# Revit family: BC_Hitachi_Cassette-RCI-FSR-1.0-6.0_LOD200
name_source: partatom
category: Mechanical Equipment
revit_build: Autodesk Revit 2018 (Build: 20170223_1515(x64)
units: mm (PartAtom-declared; Revit-internal decimal feet)

## family parameters
Cut with Voids When Loaded = No
Host = Face
OmniClass Number = 23.75.70.00
OmniClass Title = HVAC Distribution Devices
Part Type = Normal
Room Calculation Point = No
Round Connector Dimension = Use Diameter
Shared = No

## types (8) — shared parameters
BC_OBJECT_ID = 209116
BC_OBJECT_VERSION = #9
Color = Neutral white (4.56Y8.85/0.38)
Default Elevation = 1219.20 mm
Description = Standard Cassette 800*800.Individual control setting for each louver. Suitable up to 4,2 m height under ceiling . Optional motion sensor
Facade Width = 950.00 mm
Face Depth = 40.00 mm
Face Height = 950.00 mm
Frequency = 50 Hz
Manufacturer = Hitachi Air Conditioning Europe SAS
MasterFormat = Indoor Central-Station Air-Handling Units
Masterformat Code = 23 73 00
Maximal Input Power = 0 kW
Maximum AC Voltage = 253 V
Minimum AC Voltage = 207 V
Model = Cassette 800 x 800 RCI FSR
Name BIM&CO = Indoor Unit
Nominal Voltage = 230 V
Number of Poles = 1
OmniClass code = 23-33 25 00
OmniClass description = Air Handling Units
Outlet Diameter = 32.00 mm
Overall height = 840.00 mm
Overall width = 840.00 mm
Refrigerant Type = R410A / R32
Service space = Yes
Uniformat = Distribution Systems
Uniformat code = D3040
Usage Current = 5 A

## per-type parameters (varying)
| type | Acoustic Pressure Level Maxi | Acoustic Pressure Level Mini | Air Flow (HiH/Hi/Me/low) m3/min | BC_VARIANT_ID | Cooling Capacity | Fan motor input | Gas Diameter | Heating Capacity | Liquid Diameter | Mass | Maximum Air Flow | Minimum Air Flow | Overall depth | Product Code | Sound power at rated load |
| RCI-2.0FSR | 37 | 27 | 21 / 17 / 14 / 11 | 508752 | 5 kW | 57 W | 12.70 mm | 6 kW | 6.35 mm | 27.50 kg | 21000.0 L/min | 11000.0 L/min | 248.00 mm | 70405303 | 55 |
| RCI-2.5FSR | 42 | 28 | 27 / 23 / 18 / 14 | 508747 | 6 kW | 57 W | 15.88 mm | 6 kW | 9.52 mm | 28.50 kg | 27000.0 L/min | 14000.0 L/min | 248.00 mm | 70405304 | 56 |
| RCI-6.0FSR | 48 | 37 | 37 / 35 / 28 / 22 | 508746 | 14 kW | 127 W | 15.88 mm | 16 kW | 9.52 mm | 32.50 kg | 37000.0 L/min | 22000.0 L/min | 298.00 mm | 70405309 | 65 |
| RCI-5.0FSR | 48 | 35 | 37 / 33 / 26 / 21 | 508750 | 13 kW | 127 W | 15.88 mm | 14 kW | 9.52 mm | 32.50 kg | 37000.0 L/min | 21000.0 L/min | 298.00 mm | 70405308 | 64 |
| RCI-4.0FSR | 48 | 33 | 37 / 31 / 24 / 20 | 508751 | 10 kW | 127 W | 15.88 mm | 11 kW | 9.52 mm | 32.50 kg | 37000.0 L/min | 20000.0 L/min | 298.00 mm | 70405307 | 64 |
| RCI-3.0FSR | 42 | 28 | 27 / 23 / 18 / 14 | 508748 | 7 kW | 57 W | 15.88 mm | 8 kW | 9.52 mm | 32.50 kg | 27000.0 L/min | 14000.0 L/min | 298.00 mm | 70405305 | 57 |
| RCI-1.5FSR | 35 | 27 | 21 / 17 / 14 / 11 | 508749 | 4 kW | 57 W | 12.70 mm | 4 kW | 6.35 mm | 27.50 kg | 21000.0 L/min | 11000.0 L/min | 248.00 mm | 70405302 | 53 |
| RCI-1.0FSR | 33 | 27 | 15 / 13 / 11 / 9 | 508745 | 3 kW | 57 W | 12.70 mm | 3 kW | 6.35 mm | 26.50 kg | 15000.0 L/min | 9000.0 L/min | 248.00 mm | 70405301 | 52 |

note: column(s) folded — value = type name in every type: Reference, Type Comments
